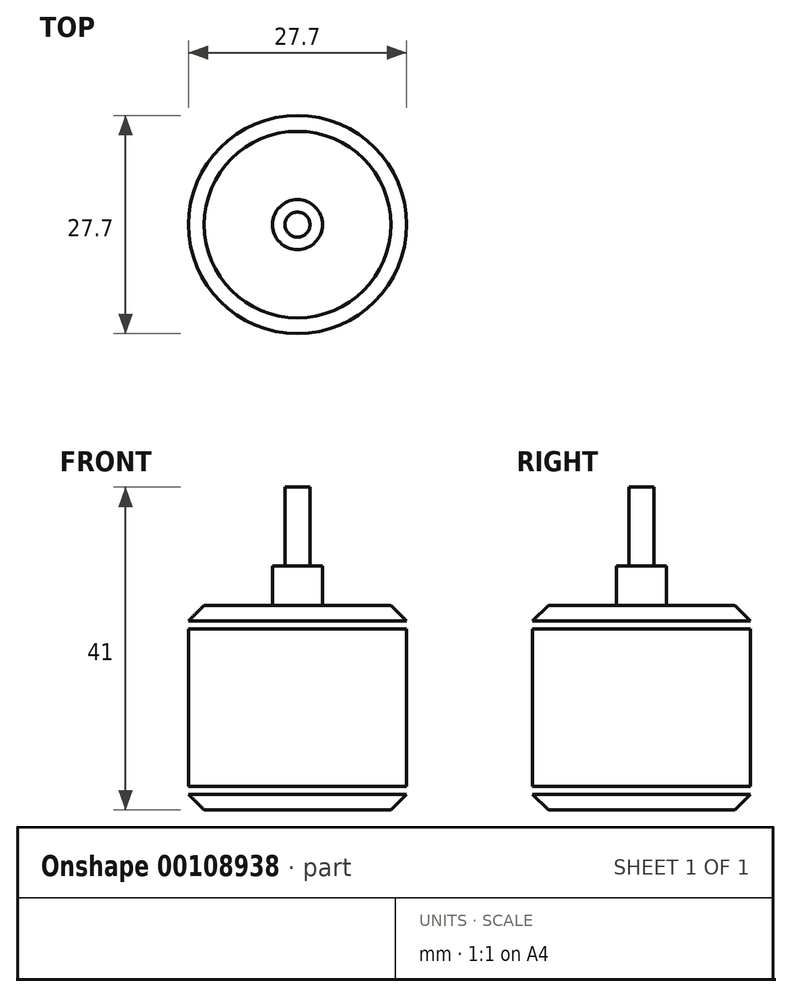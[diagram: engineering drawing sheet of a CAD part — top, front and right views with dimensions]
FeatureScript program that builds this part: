
annotation { "Feature Type Name" : "Feature", "Feature Type Description" : "" }
export const myFeature = defineFeature(function(context is Context, id is Id, definition is map)
    precondition{}
    {
        {
            var Q0;
            Q0=qCreatedBy(makeId("Front.planeOp"),FACE);
            var sketch = newSketch(context, id + "F0", { "sketchPlane" : qUnion([Q0])});
            skLineSegment(sketch, "E0", {"start": v(0, 0) * mm, "end": v(-11.85, 0) * mm});
            skLineSegment(sketch, "E1", {"start": v(-11.85, 0) * mm, "end": v(-13.85, 2) * mm});
            skLineSegment(sketch, "E2", {"start": v(-13.85, 2) * mm, "end": v(0, 2) * mm});
            skLineSegment(sketch, "E3", {"start": v(0, 2) * mm, "end": v(0, 0) * mm});
            skLineSegment(sketch, "E4.bottom", {"start": v(0, 3) * mm, "end": v(-13.85, 3) * mm});
            skLineSegment(sketch, "E4.top", {"start": v(0, 23) * mm, "end": v(-13.85, 23) * mm});
            skLineSegment(sketch, "E4.left", {"start": v(0, 3) * mm, "end": v(0, 23) * mm});
            skLineSegment(sketch, "E4.right", {"start": v(-13.85, 3) * mm, "end": v(-13.85, 23) * mm});
            skLineSegment(sketch, "E5", {"start": v(0, 24) * mm, "end": v(-13.85, 24) * mm});
            skLineSegment(sketch, "E6", {"start": v(-13.85, 24) * mm, "end": v(-11.85, 26) * mm});
            skLineSegment(sketch, "E7", {"start": v(-11.85, 26) * mm, "end": v(0, 26) * mm});
            skLineSegment(sketch, "E8", {"start": v(0, 26) * mm, "end": v(0, 24) * mm});
            skLineSegment(sketch, "E9.bottom", {"start": v(0, 26) * mm, "end": v(-3.17, 26) * mm, "construction": true});
            skLineSegment(sketch, "E9.top", {"start": v(0, 31) * mm, "end": v(-3.18, 31) * mm});
            skLineSegment(sketch, "E9.left", {"start": v(0, 26) * mm, "end": v(0, 31) * mm});
            skLineSegment(sketch, "E9.right", {"start": v(-3.17, 26) * mm, "end": v(-3.18, 31) * mm});
            skLineSegment(sketch, "E10.bottom", {"start": v(0, 31) * mm, "end": v(-1.59, 31) * mm, "construction": true});
            skLineSegment(sketch, "E10.top", {"start": v(0, 41) * mm, "end": v(-1.59, 41) * mm});
            skLineSegment(sketch, "E10.left", {"start": v(0, 31) * mm, "end": v(0, 41) * mm});
            skLineSegment(sketch, "E10.right", {"start": v(-1.59, 31) * mm, "end": v(-1.59, 41) * mm});
            skLineSegment(sketch, "E11", {"start": v(0, 3) * mm, "end": v(0, 2) * mm, "construction": true});
            skLineSegment(sketch, "E12", {"start": v(0, 23) * mm, "end": v(0, 24) * mm, "construction": true});
            skSolve(sketch);
        }
        {
            var Q0;
            Q0 = qSketchRegion(id + "F0", true);
            var Q1;
            Q1=sQuery(id+"F0.wireOp",EDGE,"E4.left");
            revolve(context, id + "F1", {"entities" : qUnion([Q0]), "axis" : qUnion([Q1]), "revolveType" : RevolveType.FULL});
        }
    });
